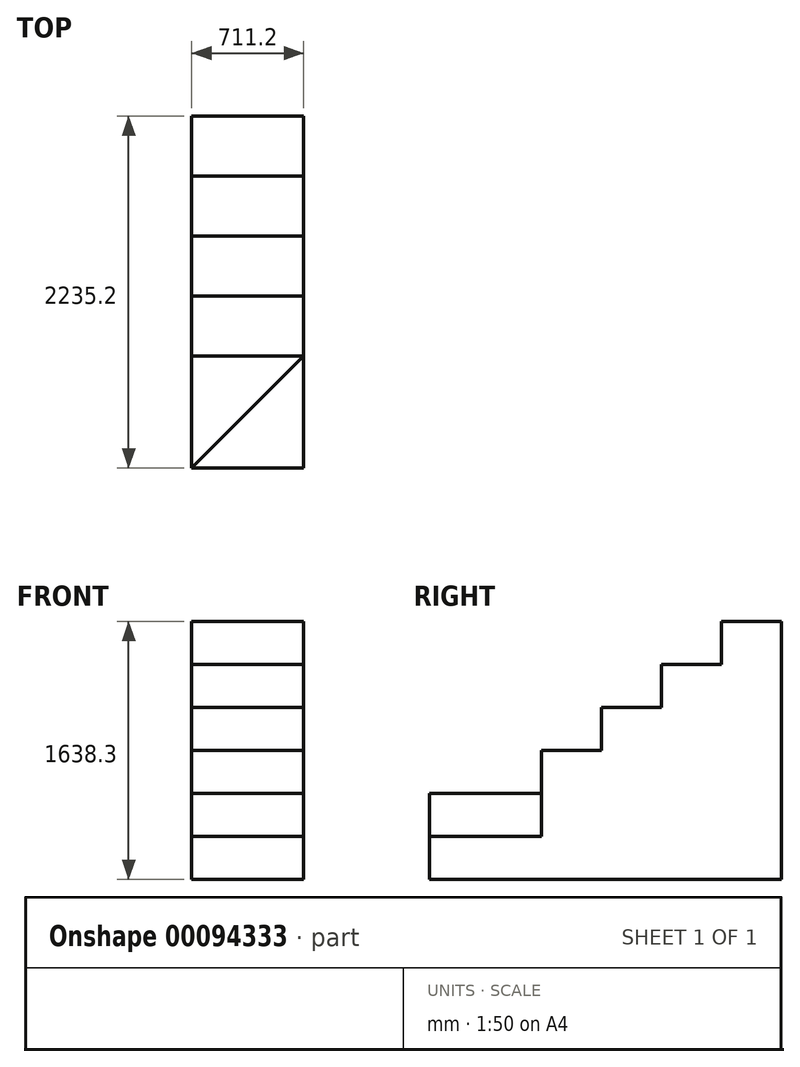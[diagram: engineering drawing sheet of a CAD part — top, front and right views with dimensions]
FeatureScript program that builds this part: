
annotation { "Feature Type Name" : "Feature", "Feature Type Description" : "" }
export const myFeature = defineFeature(function(context is Context, id is Id, definition is map)
    precondition{}
    {
        {
            var Q0;
            Q0=qCreatedBy(makeId("Top.planeOp"),FACE);
            var sketch = newSketch(context, id + "F0", { "sketchPlane" : qUnion([Q0])});
            skLineSegment(sketch, "E0.bottom", {"start": v(0, 0) * mm, "end": v(711.2, 0) * mm});
            skLineSegment(sketch, "E0.top", {"start": v(0, -2235.2) * mm, "end": v(711.2, -2235.2) * mm});
            skLineSegment(sketch, "E0.left", {"start": v(0, 0) * mm, "end": v(0, -2235.2) * mm});
            skLineSegment(sketch, "E0.right", {"start": v(711.2, 0) * mm, "end": v(711.2, -2235.2) * mm});
            skSolve(sketch);
        }
        {
            var Q0;
            Q0=makeQuery(id+"F0.imprint","IMPRINT",FACE,{"disambiguationData":[TD([[makeQuery(id+"F0.imprint","IMPRINT",EDGE,{"derivedFrom":sQuery(id+"F0.wireOp",EDGE,"E0.bottom")}),-1.0]])]});
            extrude(context, id + "F1", {"entities" : qUnion([Q0]), "depth" : 273.05 * mm});
        }
        {
            var Q0;
            Q0=makeQuery(id+"F1.opExtrude","CAP_FACE",FACE,{"disambiguationData":[OSD([sQuery(id+"F0.wireOp",EDGE,"E0.bottom"),sQuery(id+"F0.wireOp",EDGE,"E0.top"),sQuery(id+"F0.wireOp",EDGE,"E0.left"),sQuery(id+"F0.wireOp",EDGE,"E0.right")])],"isStart":false});
            var sketch = newSketch(context, id + "F2", { "sketchPlane" : qUnion([Q0])});
            skLineSegment(sketch, "E1", {"start": v(0, -2235.2) * mm, "end": v(711.2, -1524) * mm});
            skLineSegment(sketch, "E2", {"start": v(711.2, -1524) * mm, "end": v(711.2, 0) * mm});
            skLineSegment(sketch, "E3", {"start": v(711.2, 0) * mm, "end": v(0, 0) * mm});
            skLineSegment(sketch, "E4", {"start": v(0, 0) * mm, "end": v(0, -2235.2) * mm});
            skLineSegment(sketch, "E5", {"start": v(711.2, -1524) * mm, "end": v(711.2, -2235.2) * mm, "construction": true});
            skLineSegment(sketch, "E6", {"start": v(711.2, -2235.2) * mm, "end": v(0, -2235.2) * mm, "construction": true});
            skSolve(sketch);
        }
        {
            var Q0;
            Q0 = qSketchRegion(id + "F2", true);
            extrude(context, id + "F3", {"entities" : qUnion([Q0]), "operationType" : NewBodyOperationType.ADD, "depth" : 273.05 * mm});
        }
        {
            var Q0;
            Q0=makeQuery(id+"F3.opExtrude","CAP_FACE",FACE,{"disambiguationData":[OSD([sQuery(id+"F2.wireOp",EDGE,"E1"),sQuery(id+"F2.wireOp",EDGE,"E2"),sQuery(id+"F2.wireOp",EDGE,"E3"),sQuery(id+"F2.wireOp",EDGE,"E4")])],"isStart":false});
            var sketch = newSketch(context, id + "F4", { "sketchPlane" : qUnion([Q0])});
            skLineSegment(sketch, "E7.bottom", {"start": v(711.2, -1524) * mm, "end": v(0, -1524) * mm});
            skLineSegment(sketch, "E7.top", {"start": v(711.2, 0) * mm, "end": v(0, 0) * mm});
            skLineSegment(sketch, "E7.left", {"start": v(711.2, -1524) * mm, "end": v(711.2, 0) * mm});
            skLineSegment(sketch, "E7.right", {"start": v(0, -1524) * mm, "end": v(0, 0) * mm});
            skSolve(sketch);
        }
        {
            var Q0;
            Q0 = qSketchRegion(id + "F4", true);
            extrude(context, id + "F5", {"entities" : qUnion([Q0]), "operationType" : NewBodyOperationType.ADD, "depth" : 273.05 * mm});
        }
        {
            var Q0;
            Q0=makeQuery(id+"F5.opExtrude","CAP_FACE",FACE,{"disambiguationData":[OSD([sQuery(id+"F4.wireOp",EDGE,"E7.bottom"),sQuery(id+"F4.wireOp",EDGE,"E7.top"),sQuery(id+"F4.wireOp",EDGE,"E7.left"),sQuery(id+"F4.wireOp",EDGE,"E7.right")])],"isStart":false});
            var sketch = newSketch(context, id + "F6", { "sketchPlane" : qUnion([Q0])});
            skLineSegment(sketch, "E8.bottom", {"start": v(711.2, 0) * mm, "end": v(0, 0) * mm});
            skLineSegment(sketch, "E8.top", {"start": v(711.2, -1143) * mm, "end": v(0, -1143) * mm});
            skLineSegment(sketch, "E8.left", {"start": v(711.2, 0) * mm, "end": v(711.2, -1143) * mm});
            skLineSegment(sketch, "E8.right", {"start": v(0, 0) * mm, "end": v(0, -1143) * mm});
            skSolve(sketch);
        }
        {
            var Q0;
            Q0=makeQuery(id+"F6.imprint","IMPRINT",FACE,{"disambiguationData":[TD([[makeQuery(id+"F6.imprint","IMPRINT",EDGE,{"derivedFrom":sQuery(id+"F6.wireOp",EDGE,"E8.bottom")}),-1.0]])]});
            extrude(context, id + "F7", {"entities" : qUnion([Q0]), "operationType" : NewBodyOperationType.ADD, "depth" : 273.05 * mm});
        }
        {
            var Q0;
            Q0=makeQuery(id+"F7.opExtrude","CAP_FACE",FACE,{"disambiguationData":[OSD([sQuery(id+"F6.wireOp",EDGE,"E8.bottom"),sQuery(id+"F6.wireOp",EDGE,"E8.top"),sQuery(id+"F6.wireOp",EDGE,"E8.left"),sQuery(id+"F6.wireOp",EDGE,"E8.right")])],"isStart":false});
            var sketch = newSketch(context, id + "F8", { "sketchPlane" : qUnion([Q0])});
            skLineSegment(sketch, "E9.bottom", {"start": v(711.2, -762) * mm, "end": v(0, -762) * mm});
            skLineSegment(sketch, "E9.top", {"start": v(711.2, 0) * mm, "end": v(0, 0) * mm});
            skLineSegment(sketch, "E9.left", {"start": v(711.2, -762) * mm, "end": v(711.2, 0) * mm});
            skLineSegment(sketch, "E9.right", {"start": v(0, -762) * mm, "end": v(0, 0) * mm});
            skLineSegment(sketch, "E10", {"start": v(711.2, -1143) * mm, "end": v(711.2, -762) * mm, "construction": true});
            skSolve(sketch);
        }
        {
            var Q0;
            Q0 = qSketchRegion(id + "F8", true);
            extrude(context, id + "F9", {"entities" : qUnion([Q0]), "operationType" : NewBodyOperationType.ADD, "depth" : 273.05 * mm});
        }
        {
            var Q0;
            Q0=makeQuery(id+"F9.opExtrude","CAP_FACE",FACE,{"disambiguationData":[OSD([sQuery(id+"F8.wireOp",EDGE,"E9.bottom"),sQuery(id+"F8.wireOp",EDGE,"E9.top"),sQuery(id+"F8.wireOp",EDGE,"E9.left"),sQuery(id+"F8.wireOp",EDGE,"E9.right")])],"isStart":false});
            var sketch = newSketch(context, id + "F10", { "sketchPlane" : qUnion([Q0])});
            skLineSegment(sketch, "E11.bottom", {"start": v(711.2, -381) * mm, "end": v(0, -381) * mm});
            skLineSegment(sketch, "E11.top", {"start": v(711.2, 0) * mm, "end": v(0, 0) * mm});
            skLineSegment(sketch, "E11.left", {"start": v(711.2, -381) * mm, "end": v(711.2, 0) * mm});
            skLineSegment(sketch, "E11.right", {"start": v(0, -381) * mm, "end": v(0, 0) * mm});
            skLineSegment(sketch, "E12", {"start": v(711.2, -762) * mm, "end": v(711.2, -381) * mm, "construction": true});
            skSolve(sketch);
        }
        {
            var Q0;
            Q0 = qSketchRegion(id + "F10", true);
            extrude(context, id + "F11", {"entities" : qUnion([Q0]), "operationType" : NewBodyOperationType.ADD, "depth" : 273.05 * mm});
        }
    });
